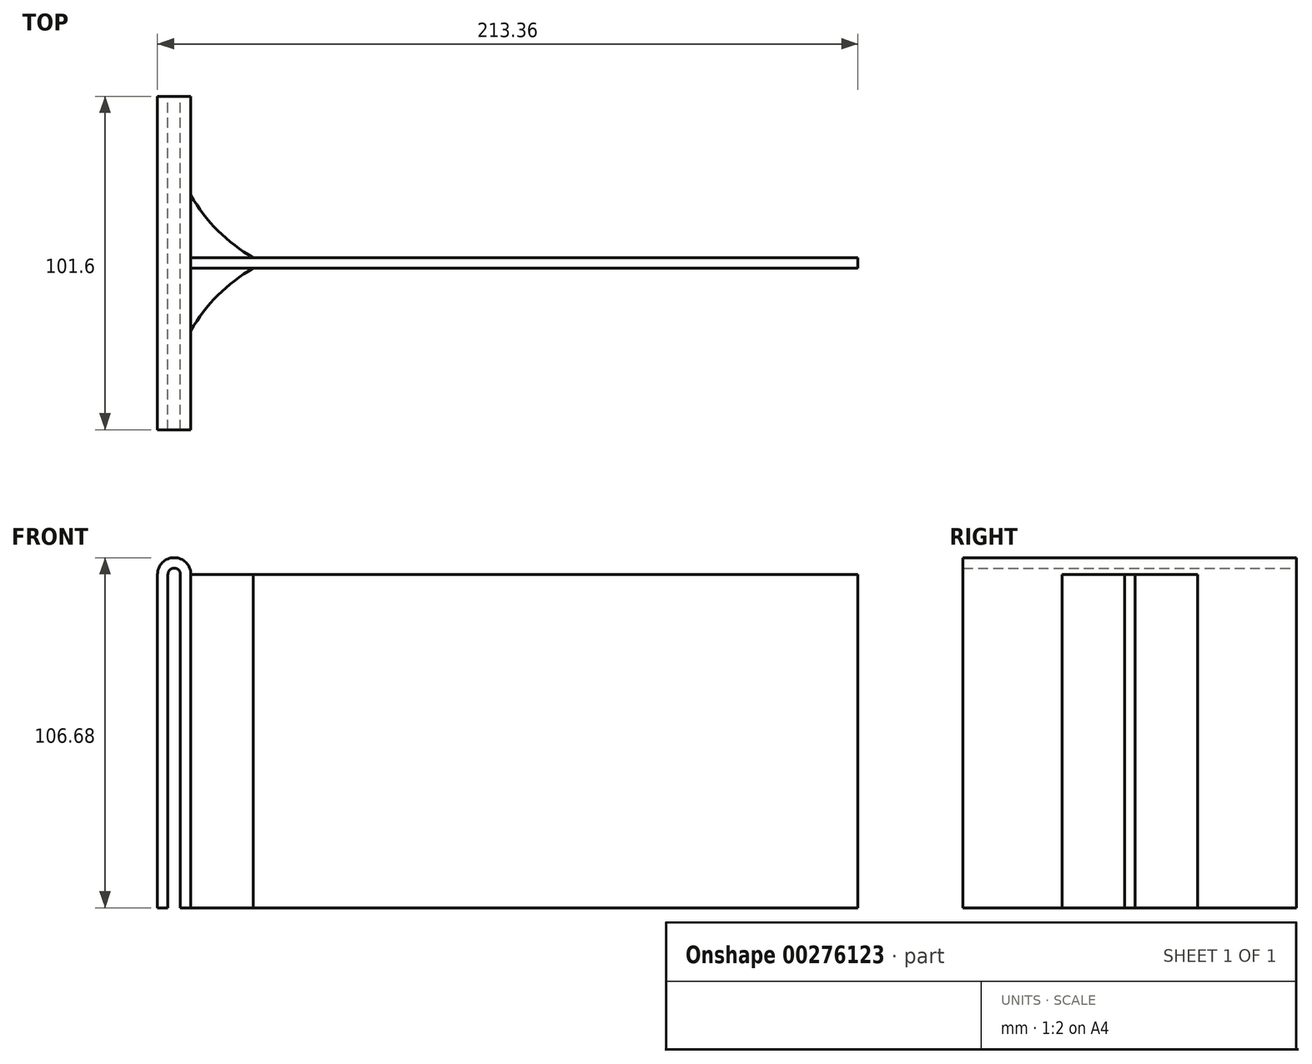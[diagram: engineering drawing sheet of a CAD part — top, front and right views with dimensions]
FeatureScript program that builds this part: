
annotation { "Feature Type Name" : "Feature", "Feature Type Description" : "" }
export const myFeature = defineFeature(function(context is Context, id is Id, definition is map)
    precondition{}
    {
        {
            var Q0;
            Q0=qCreatedBy(makeId("Front.planeOp"),FACE);
            var sketch = newSketch(context, id + "F0", { "sketchPlane" : qUnion([Q0])});
            skLineSegment(sketch, "E0.bottom", {"start": v(0, 0) * mm, "end": v(203.2, 0) * mm});
            skLineSegment(sketch, "E0.top", {"start": v(0, 101.6) * mm, "end": v(203.2, 101.6) * mm});
            skLineSegment(sketch, "E0.left", {"start": v(0, 0) * mm, "end": v(0, 101.6) * mm});
            skLineSegment(sketch, "E0.right", {"start": v(203.2, 0) * mm, "end": v(203.2, 101.6) * mm});
            skSolve(sketch);
        }
        {
            var Q0;
            Q0 = qSketchRegion(id + "F0", true);
            extrude(context, id + "F1", {"entities" : qUnion([Q0]), "endBound" : BoundingType.SYMMETRIC, "depth" : 3.17 * mm});
        }
        {
            var Q0;
            Q0=qCreatedBy(makeId("Front.planeOp"),FACE);
            var sketch = newSketch(context, id + "F2", { "sketchPlane" : qUnion([Q0])});
            skLineSegment(sketch, "E1.bottom", {"start": v(0, 0) * mm, "end": v(-3.17, 0) * mm});
            skLineSegment(sketch, "E1.left", {"start": v(0, 0) * mm, "end": v(0, 101.6) * mm});
            skLineSegment(sketch, "E1.right", {"start": v(-3.17, 0) * mm, "end": v(-3.17, 101.6) * mm});
            skLineSegment(sketch, "E2.bottom", {"start": v(-6.98, 0) * mm, "end": v(-10.16, 0) * mm});
            skLineSegment(sketch, "E2.left", {"start": v(-6.99, 0) * mm, "end": v(-6.99, 101.6) * mm});
            skLineSegment(sketch, "E2.right", {"start": v(-10.16, 0) * mm, "end": v(-10.16, 101.6) * mm});
            skArc(sketch, "E3", {"start": v(0, 101.6) * mm, "mid": v(-5.08, 106.68) * mm, "end": v(-10.16, 101.6) * mm});
            skArc(sketch, "E4", {"start": v(-3.17, 101.6) * mm, "mid": v(-5.08, 103.5) * mm, "end": v(-6.99, 101.6) * mm});
            skSolve(sketch);
        }
        {
            var Q0;
            Q0 = qSketchRegion(id + "F2", true);
            extrude(context, id + "F3", {"entities" : qUnion([Q0]), "endBound" : BoundingType.SYMMETRIC, "depth" : 101.6 * mm});
        }
        {
            var Q0;
            Q0=qCreatedBy(makeId("Top.planeOp"),FACE);
            var sketch = newSketch(context, id + "F4", { "sketchPlane" : qUnion([Q0])});
            skPoint(sketch, "E5.0", {"position": v(0, -1.59) * mm});
            skLineSegment(sketch, "E6", {"start": v(0, -20.64) * mm, "end": v(0, -1.59) * mm});
            skLineSegment(sketch, "E7", {"start": v(0, -1.59) * mm, "end": v(19.05, -1.59) * mm});
            skArc(sketch, "E8", {"start": v(19.05, -1.59) * mm, "mid": v(8.24, -9.83) * mm, "end": v(0, -20.64) * mm});
            skSolve(sketch);
        }
        {
            var Q0;
            Q0 = qSketchRegion(id + "F4", true);
            var Q1;
            Q1=makeQuery(id+"F1.opExtrude","SWEPT_FACE",FACE,{"disambiguationData":[OSD([sQuery(id+"F0.wireOp",EDGE,"E0.top")])]});
            extrude(context, id + "F5", {"entities" : qUnion([Q0]), "endBound" : BoundingType.UP_TO_SURFACE, "endBoundEntityFace" : qUnion([Q1]), "depth" : 25.4 * mm});
        }
        {
            var Q0;
            Q0=makeQuery(id+"F5.opExtrude","SWEPT_BODY",BODY,{"disambiguationData":[OSD([sQuery(id+"F4.wireOp",EDGE,"E6"),sQuery(id+"F4.wireOp",EDGE,"E7"),sQuery(id+"F4.wireOp",EDGE,"E8")])]});
            var Q1;
            Q1=qCreatedBy(makeId("Front.planeOp"),FACE);
            mirror(context, id + "F6", {"entities" : qUnion([Q0]), "mirrorPlane" : qUnion([Q1])});
        }
    });
